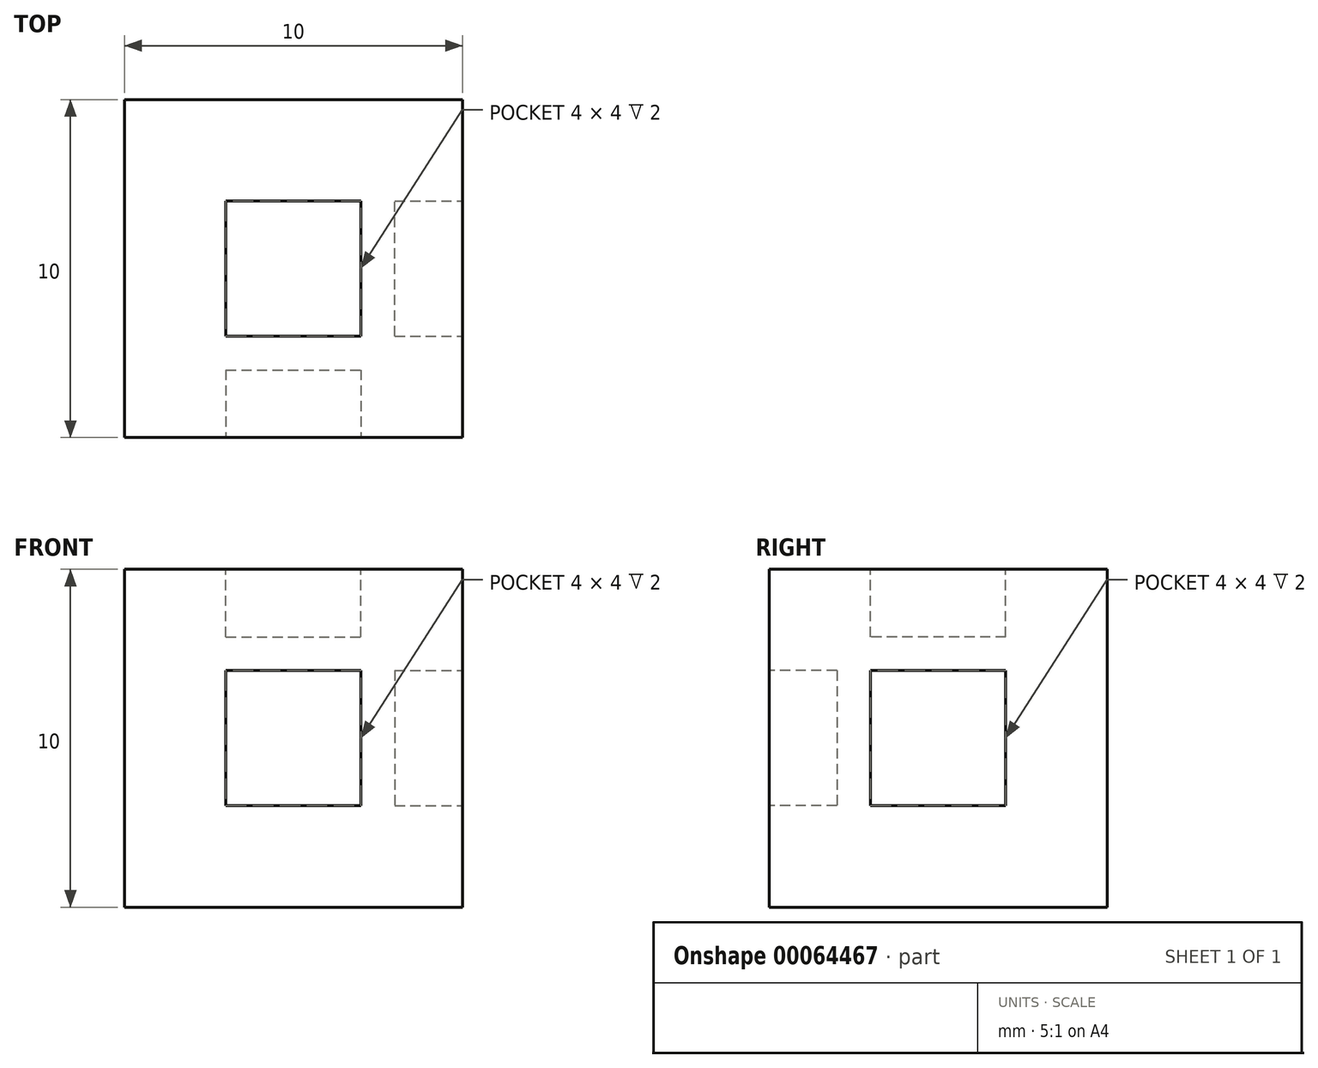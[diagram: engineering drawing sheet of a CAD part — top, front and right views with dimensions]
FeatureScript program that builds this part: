
annotation { "Feature Type Name" : "Feature", "Feature Type Description" : "" }
export const myFeature = defineFeature(function(context is Context, id is Id, definition is map)
    precondition{}
    {
        {
            var Q0;
            Q0=qCreatedBy(makeId("Top.planeOp"),FACE);
            var sketch = newSketch(context, id + "F0", { "sketchPlane" : qUnion([Q0])});
            skLineSegment(sketch, "E0.rect.bottom", {"start": v(5, -5) * mm, "end": v(-5, -5) * mm});
            skLineSegment(sketch, "E0.rect.top", {"start": v(5, 5) * mm, "end": v(-5, 5) * mm});
            skLineSegment(sketch, "E0.rect.left", {"start": v(5, -5) * mm, "end": v(5, 5) * mm});
            skLineSegment(sketch, "E0.rect.right", {"start": v(-5, -5) * mm, "end": v(-5, 5) * mm});
            skPoint(sketch, "E0.rect.middle", {"position": v(0, 0) * mm});
            skSolve(sketch);
        }
        {
            var Q0;
            Q0=makeQuery(id+"F0.imprint","IMPRINT",FACE,{"disambiguationData":[TD([[makeQuery(id+"F0.imprint","IMPRINT",EDGE,{"derivedFrom":sQuery(id+"F0.wireOp",EDGE,"E0.rect.bottom")}),-1.0]])]});
            extrude(context, id + "F1", {"entities" : qUnion([Q0]), "depth" : 10 * mm});
        }
        {
            var Q0;
            Q0=makeQuery(id+"F1.opExtrude","SWEPT_FACE",FACE,{"disambiguationData":[OSD([sQuery(id+"F0.wireOp",EDGE,"E0.rect.left")])]});
            var sketch = newSketch(context, id + "F2", { "sketchPlane" : qUnion([Q0])});
            skLineSegment(sketch, "E1.0", {"start": v(-2, 3) * mm, "end": v(2, 3) * mm});
            skLineSegment(sketch, "E1.1", {"start": v(-2, 7) * mm, "end": v(-2, 3) * mm});
            skLineSegment(sketch, "E1.2", {"start": v(2, 7) * mm, "end": v(-2, 7) * mm});
            skLineSegment(sketch, "E1.3", {"start": v(2, 3) * mm, "end": v(2, 7) * mm});
            skSolve(sketch);
        }
        {
            var Q0;
            Q0=makeQuery(id+"F2.imprint","IMPRINT",FACE,{"disambiguationData":[TD([[makeQuery(id+"F2.imprint","IMPRINT",EDGE,{"derivedFrom":sQuery(id+"F2.wireOp",EDGE,"E1.0")}),1.0]])]});
            extrude(context, id + "F3", {"entities" : qUnion([Q0]), "operationType" : NewBodyOperationType.REMOVE, "oppositeDirection" : true, "depth" : 2 * mm});
        }
        {
            var Q0;
            Q0=makeQuery(id+"F1.opExtrude","SWEPT_FACE",FACE,{"disambiguationData":[OSD([sQuery(id+"F0.wireOp",EDGE,"E0.rect.bottom")])]});
            var sketch = newSketch(context, id + "F4", { "sketchPlane" : qUnion([Q0])});
            skLineSegment(sketch, "E2.0", {"start": v(-2, 3) * mm, "end": v(2, 3) * mm});
            skLineSegment(sketch, "E2.1", {"start": v(-2, 7) * mm, "end": v(-2, 3) * mm});
            skLineSegment(sketch, "E2.2", {"start": v(2, 7) * mm, "end": v(-2, 7) * mm});
            skLineSegment(sketch, "E2.3", {"start": v(2, 3) * mm, "end": v(2, 7) * mm});
            skSolve(sketch);
        }
        {
            var Q0;
            Q0=makeQuery(id+"F1.opExtrude","CAP_FACE",FACE,{"disambiguationData":[OSD([sQuery(id+"F0.wireOp",EDGE,"E0.rect.bottom"),sQuery(id+"F0.wireOp",EDGE,"E0.rect.top"),sQuery(id+"F0.wireOp",EDGE,"E0.rect.left"),sQuery(id+"F0.wireOp",EDGE,"E0.rect.right")])],"isStart":false});
            var sketch = newSketch(context, id + "F5", { "sketchPlane" : qUnion([Q0])});
            skLineSegment(sketch, "E3.0", {"start": v(-2, -2) * mm, "end": v(2, -2) * mm});
            skLineSegment(sketch, "E3.1", {"start": v(-2, 2) * mm, "end": v(-2, -2) * mm});
            skLineSegment(sketch, "E3.2", {"start": v(2, 2) * mm, "end": v(-2, 2) * mm});
            skLineSegment(sketch, "E3.3", {"start": v(2, -2) * mm, "end": v(2, 2) * mm});
            skSolve(sketch);
        }
        {
            var Q0;
            Q0=makeQuery(id+"F4.imprint","IMPRINT",FACE,{"disambiguationData":[TD([[makeQuery(id+"F4.imprint","IMPRINT",EDGE,{"derivedFrom":sQuery(id+"F4.wireOp",EDGE,"E2.0")}),1.0]])]});
            extrude(context, id + "F6", {"entities" : qUnion([Q0]), "operationType" : NewBodyOperationType.REMOVE, "oppositeDirection" : true, "depth" : 2 * mm});
        }
        {
            var Q0;
            Q0=makeQuery(id+"F5.imprint","IMPRINT",FACE,{"disambiguationData":[TD([[makeQuery(id+"F5.imprint","IMPRINT",EDGE,{"derivedFrom":sQuery(id+"F5.wireOp",EDGE,"E3.0")}),1.0]])]});
            extrude(context, id + "F7", {"entities" : qUnion([Q0]), "operationType" : NewBodyOperationType.REMOVE, "oppositeDirection" : true, "depth" : 2 * mm});
        }
    });
